# Revit family: Tere
name_source: partatom
category: Furniture
revit_build: Autodesk Revit 2015 (Build: 20140606_1530(x64)
units: mm (PartAtom-declared; Revit-internal decimal feet)

## types (10) — shared parameters
Armrest material = Black
Footpad material = Rubber, Black
Frame material = Steel, chrome
Manufacturer = Isku Oy
Type Comments = Available as antimicrobial
URL = www.isku.fi

## per-type parameters (varying)
| type | Arms | Upholstery material | Width |
| Tere 3738 sofa 2-persons width 1180mm - with armrest | Yes | Fabric - Green | 1180 mm  [stored 3.87139 ft] |
| Tere 3738 sofa 2-persons width 1180mm - no armrest | No | Fabric - Green | 1180 mm  [stored 3.87139 ft] |
| Tere 3738 sofa 2-persons width 1420mm - with armrest | Yes | Leather - white | 1420 mm |
| Tere 3738 sofa 2-persons width 1420mm - no armrest | No | Leather - white | 1420 mm |
| Tere 3738 sofa 3-persons width 1760mm - with armrest | Yes | Fabric - Yellow | 1760 mm  [stored 5.77428 ft] |
| Tere 3738 sofa 3-persons width 1760mm - no armrest | No | Fabric - Yellow | 1760 mm  [stored 5.77428 ft] |
| Tere 3738 sofa 3-persons width 2000mm - with armrest | Yes | Fabric - Blue | 2000 mm  [stored 6.56168 ft] |
| Tere 3738 sofa 3-persons width 2000mm - no armrest | No | Fabric - Blue | 2000 mm  [stored 6.56168 ft] |
| Tere 3738 chair width 610mm - no armrest | No | Fabric - Green | 610 mm  [stored 2.00131 ft] |
| Tere 3738 chair width 610mm - with armrest | Yes | Fabric - Green | 610 mm  [stored 2.00131 ft] |

note: [stored X ft] marks values corroborated as IEEE doubles in the binary element streams (Revit-internal decimal feet)

## geometry (parser evidence)
native form markers: Sweep x6
no freeform markers — native parametric forms only
